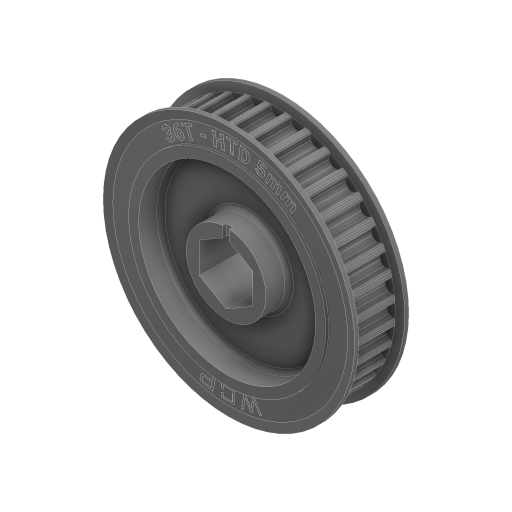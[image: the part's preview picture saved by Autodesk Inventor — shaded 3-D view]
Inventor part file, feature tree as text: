
AUTODESK INVENTOR PART (.ipt)
format: ipt  version: 2024 (Build 280153000, 153)  size: 1,101,312 bytes
history: native  units: in
note: dims shown in document units (in); Inventor stores cm internally (conversion verified against a paired STEP export)
features: mirror x2, other x1
ambient origin geometry x8: Origin, YZ Plane, XZ Plane, XY Plane, X Axis, Y Axis, Z Axis, Center Point
bodies: Solid1 (feature_tree), Solid2 (feature_tree), Solid3 (feature_tree)
feature tree (3):
  mirror  "Mirror1"
  mirror  "Mirror1:1"
  other  "Cut-Extrude5"
